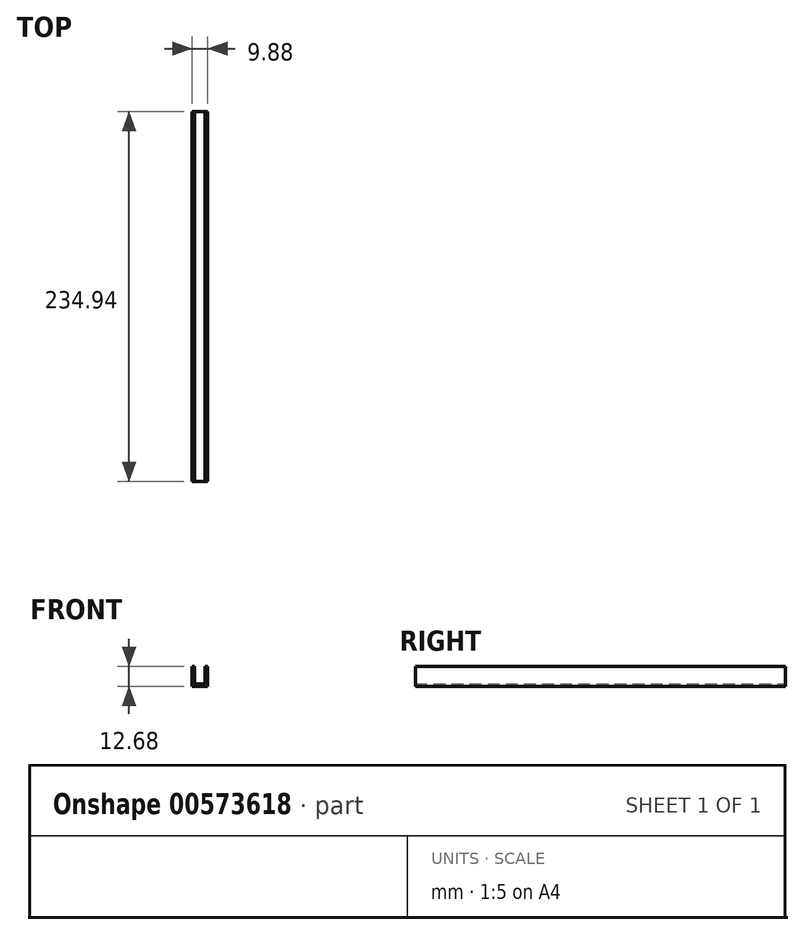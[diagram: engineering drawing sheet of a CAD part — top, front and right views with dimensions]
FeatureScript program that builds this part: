
annotation { "Feature Type Name" : "Feature", "Feature Type Description" : "" }
export const myFeature = defineFeature(function(context is Context, id is Id, definition is map)
    precondition{}
    {
        {
            var Q0;
            Q0=qCreatedBy(makeId("Front.planeOp"),FACE);
            var sketch = newSketch(context, id + "F0", { "sketchPlane" : qUnion([Q0])});
            skLineSegment(sketch, "E0", {"start": v(-4.94, 0) * mm, "end": v(4.94, 0) * mm});
            skLineSegment(sketch, "E1", {"start": v(4.95, 0) * mm, "end": v(4.95, 12.68) * mm});
            skLineSegment(sketch, "E2", {"start": v(4.94, 12.68) * mm, "end": v(3.33, 12.68) * mm});
            skLineSegment(sketch, "E3", {"start": v(3.33, 12.68) * mm, "end": v(3.34, 1.6) * mm});
            skLineSegment(sketch, "E4", {"start": v(3.34, 1.61) * mm, "end": v(-3.34, 1.6) * mm});
            skLineSegment(sketch, "E5", {"start": v(-3.34, 1.6) * mm, "end": v(-3.34, 12.68) * mm});
            skLineSegment(sketch, "E6", {"start": v(-3.34, 12.68) * mm, "end": v(-4.94, 12.68) * mm});
            skLineSegment(sketch, "E7", {"start": v(-4.95, 12.68) * mm, "end": v(-4.94, 0) * mm});
            skLineSegment(sketch, "E8", {"start": v(-3.34, 1.6) * mm, "end": v(-3.34, 0) * mm, "construction": true});
            skSolve(sketch);
        }
        {
            var Q0;
            Q0 = qSketchRegion(id + "F0", true);
            extrude(context, id + "F1", {"entities" : qUnion([Q0]), "endBound" : BoundingType.SYMMETRIC, "depth" : 234.95 * mm, "offsetDistance" : 25 * mm});
        }
    });
